# Revit family: Toilet_Seat-Elongated_Closed_Front-KOHLER-Veil-K-77471IN
name_source: partatom
category: Specialty Equipment
units: mm (PartAtom-declared; Revit-internal decimal feet)

## family parameters
Cut with Voids When Loaded = No
Host = Face
Maintain Annotation Orientation = No
OmniClass Number = 23.31.19.19.17
Part Type = Normal
Room Calculation Point = No
Round Connector Dimension = Use Diameter
Shared = No

## types (3) — shared parameters
ADA Compliant = No
Assembly Code = C1030200
Date Modified = 12/31/2023
Default Elevation = 15"
Height = 2 1/8"
Length = 19 1/4"
Manufacturer = Kohler Co.
Master Format 2014 = 10 28 00
Master Format 2014 Name = Toilet, Bath, and Laundry Accessories
Material = Plastic
Product Name = Veil
URL = https://www.kohler.co.in
WaterSense Certified = No
Width = 14 11/16"

## per-type parameters (varying)
| type | Description | Finish | Model | Type |
| DGS-Indigo | Wall Hung Quite Close UF Seat Black | Kohler-Plastic-DGS-Indigo | K-77471IN-DGS | 1 |
| 7-Black Black | Wall Hung Quite Close UF Seat Black | Kohler-Plastic-7-Black_Black | K-77471IN-7 | 2 |
| 0-White | Wall Hung Quite Close UF Seat Indigo | Kohler-Plastic-0-White | K-77471IN-0 | 3 |

## geometry (parser evidence)
native form markers: Sweep x4
no freeform markers — native parametric forms only
